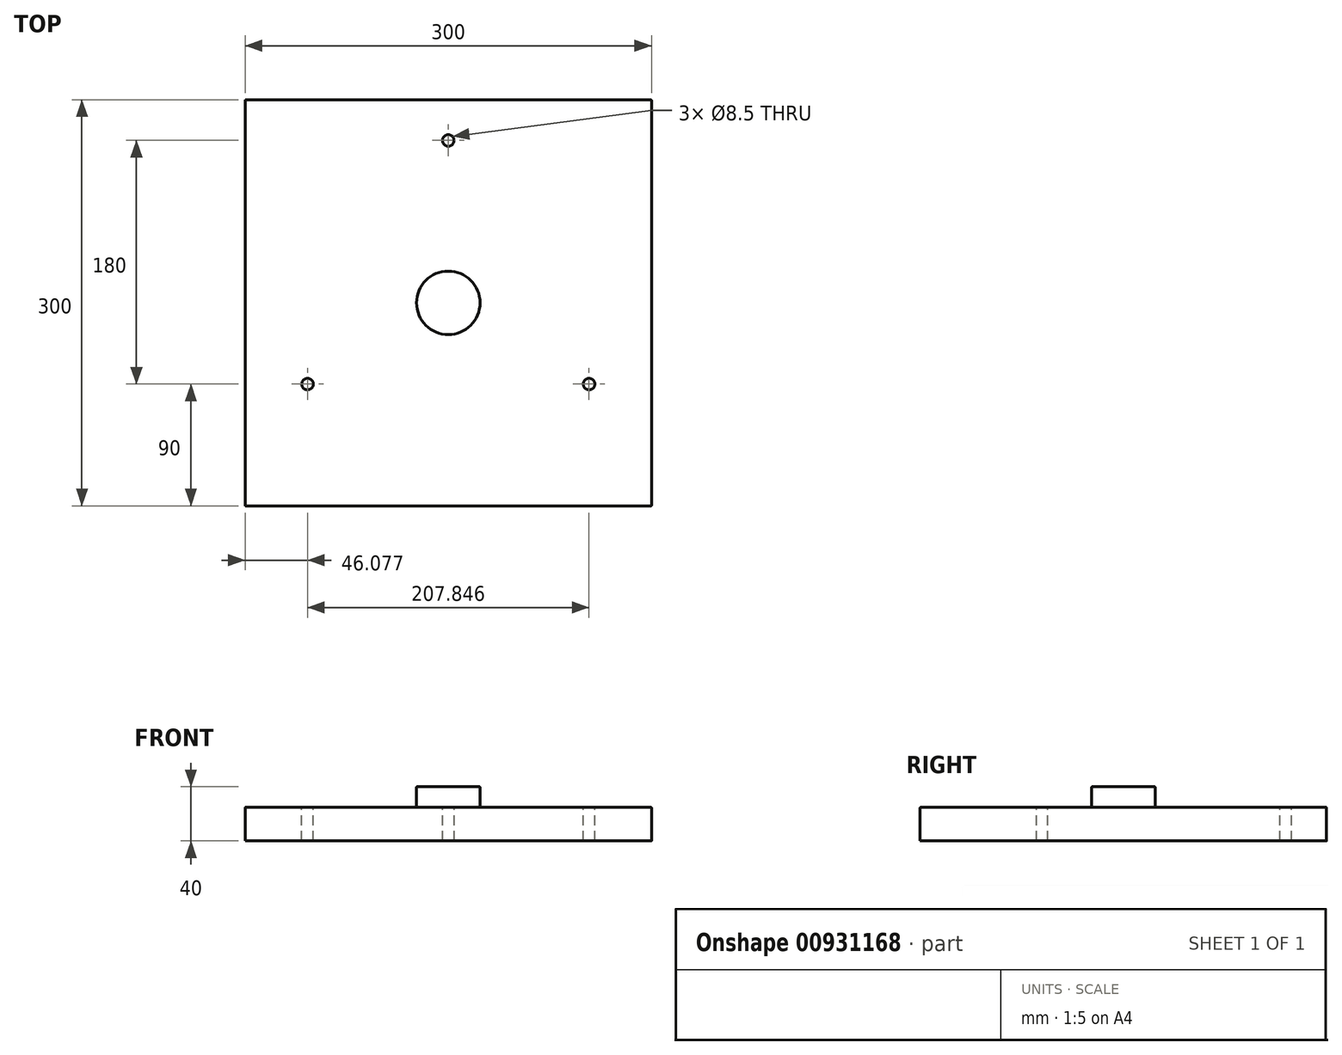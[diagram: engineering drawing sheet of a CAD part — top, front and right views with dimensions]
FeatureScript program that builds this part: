
annotation { "Feature Type Name" : "Feature", "Feature Type Description" : "" }
export const myFeature = defineFeature(function(context is Context, id is Id, definition is map)
    precondition{}
    {
        {
            var Q0;
            Q0=qCreatedBy(makeId("Top.planeOp"),FACE);
            var sketch = newSketch(context, id + "F0", { "sketchPlane" : qUnion([Q0])});
            skLineSegment(sketch, "E0.bottom", {"start": v(150, 150) * mm, "end": v(-150, 150) * mm});
            skLineSegment(sketch, "E0.top", {"start": v(150, -150) * mm, "end": v(-150, -150) * mm});
            skLineSegment(sketch, "E0.left", {"start": v(150, 150) * mm, "end": v(150, -150) * mm});
            skLineSegment(sketch, "E0.right", {"start": v(-150, 150) * mm, "end": v(-150, -150) * mm});
            skPoint(sketch, "E0.middle", {"position": v(0, 0) * mm});
            skSolve(sketch);
        }
        {
            var Q0;
            Q0=makeQuery(id+"F0.imprint","IMPRINT",FACE,{"disambiguationData":[TD([[makeQuery(id+"F0.imprint","IMPRINT",EDGE,{"derivedFrom":sQuery(id+"F0.wireOp",EDGE,"E0.bottom")}),1.0]])]});
            extrude(context, id + "F1", {"entities" : qUnion([Q0]), "depth" : 25 * mm, "offsetDistance" : 25 * mm});
        }
        {
            var Q0;
            Q0=makeQuery(id+"F1.opExtrude","CAP_FACE",FACE,{"disambiguationData":[OSD([sQuery(id+"F0.wireOp",EDGE,"E0.bottom"),sQuery(id+"F0.wireOp",EDGE,"E0.top"),sQuery(id+"F0.wireOp",EDGE,"E0.left"),sQuery(id+"F0.wireOp",EDGE,"E0.right")])],"isStart":false});
            var sketch = newSketch(context, id + "F2", { "sketchPlane" : qUnion([Q0])});
            skCircle(sketch, "E1", {"center": v(0, 0) * mm, "radius": 23.45 * mm});
            skSolve(sketch);
        }
        {
            var Q0;
            Q0=makeQuery(id+"F2.imprint","IMPRINT",FACE,{"disambiguationData":[TD([[makeQuery(id+"F2.imprint","IMPRINT",EDGE,{"derivedFrom":sQuery(id+"F2.wireOp",EDGE,"E1")}),1.0]])]});
            extrude(context, id + "F3", {"entities" : qUnion([Q0]), "operationType" : NewBodyOperationType.ADD, "depth" : 15 * mm, "offsetDistance" : 25 * mm});
        }
        {
            var Q0;
            Q0=makeQuery(id+"F1.opExtrude","CAP_FACE",FACE,{"disambiguationData":[OSD([sQuery(id+"F0.wireOp",EDGE,"E0.bottom"),sQuery(id+"F0.wireOp",EDGE,"E0.top"),sQuery(id+"F0.wireOp",EDGE,"E0.left"),sQuery(id+"F0.wireOp",EDGE,"E0.right")])],"isStart":false});
            var sketch = newSketch(context, id + "F4", { "sketchPlane" : qUnion([Q0])});
            skCircle(sketch, "E2", {"center": v(0, 0) * mm, "radius": 120 * mm, "construction": true});
            skLineSegment(sketch, "E3", {"start": v(0, 0) * mm, "end": v(0, 132.8) * mm, "construction": true});
            skLineSegment(sketch, "E4", {"start": v(0, 0) * mm, "end": v(127.4, -73.56) * mm, "construction": true});
            skLineSegment(sketch, "E5", {"start": v(0, 0) * mm, "end": v(-131.87, -76.14) * mm, "construction": true});
            skPoint(sketch, "E6", {"position": v(0, 120) * mm});
            skPoint(sketch, "E7", {"position": v(103.92, -60) * mm});
            skPoint(sketch, "E8", {"position": v(-103.92, -60) * mm});
            skSolve(sketch);
        }
        {
            var Q0;
            Q0=sQuery(id+"F4.wireOp",VERTEX,"E6");
            var Q1;
            Q1=sQuery(id+"F4.wireOp",VERTEX,"E7");
            var Q2;
            Q2=sQuery(id+"F4.wireOp",VERTEX,"E8");
            var Q3;
            Q3=makeQuery(id+"F1.opExtrude","SWEPT_BODY",BODY,{"disambiguationData":[OSD([sQuery(id+"F0.wireOp",EDGE,"E0.bottom"),sQuery(id+"F0.wireOp",EDGE,"E0.top"),sQuery(id+"F0.wireOp",EDGE,"E0.left"),sQuery(id+"F0.wireOp",EDGE,"E0.right")])]});
            hole(context, id + "F5", {"style" : HoleStyle.SIMPLE, "endStyle" : HoleEndStyle.THROUGH, "standardTappedOrClearance" : lookupTablePath({ "standard" : "ISO", "engagement" : "75%", "pitch" : "1.5 mm", "size" : "M10", "type" : "Tapped" }), "standardBlindInLast" : lookupTablePath({ "standard" : "ISO", "engagement" : "75%", "pitch" : "1.5 mm", "size" : "M10", "type" : "Tapped" }), "holeDiameter" : 8.5 * mm, "majorDiameter" : 10 * mm, "showTappedDepth" : true, "isTappedThrough" : true, "tappedDepth" : 12 * mm, "tapClearance" : 3, "locations" : qUnion([Q0, Q1, Q2]), "scope" : qUnion([Q3])});
        }
        {
            var Q0;
            Q0=makeQuery(id+"F3.opExtrude","CAP_EDGE",EDGE,{"disambiguationData":[OSD([sQuery(id+"F2.wireOp",EDGE,"E1")])],"isStart":false});
            var Q1;
            Q1=makeQuery(id+"F1.opExtrude","CAP_FACE",FACE,{"disambiguationData":[OSD([sQuery(id+"F0.wireOp",EDGE,"E0.bottom"),sQuery(id+"F0.wireOp",EDGE,"E0.top"),sQuery(id+"F0.wireOp",EDGE,"E0.left"),sQuery(id+"F0.wireOp",EDGE,"E0.right")])],"isStart":false});
            var Q2;
            Q2=makeQuery(id+"F1.opExtrude","SWEPT_EDGE",EDGE,{"disambiguationData":[OSD([sQuery(id+"F0.wireOp",EDGE,"E0.top"),sQuery(id+"F0.wireOp",EDGE,"E0.left")])]});
            var Q3;
            Q3=makeQuery(id+"F1.opExtrude","SWEPT_EDGE",EDGE,{"disambiguationData":[OSD([sQuery(id+"F0.wireOp",EDGE,"E0.bottom"),sQuery(id+"F0.wireOp",EDGE,"E0.left")])]});
            var Q4;
            Q4=makeQuery(id+"F1.opExtrude","SWEPT_EDGE",EDGE,{"disambiguationData":[OSD([sQuery(id+"F0.wireOp",EDGE,"E0.top"),sQuery(id+"F0.wireOp",EDGE,"E0.right")])]});
            var Q5;
            Q5=makeQuery(id+"F1.opExtrude","SWEPT_EDGE",EDGE,{"disambiguationData":[OSD([sQuery(id+"F0.wireOp",EDGE,"E0.bottom"),sQuery(id+"F0.wireOp",EDGE,"E0.right")])]});
            fillet(context, id + "F6", {"entities" : qUnion([Q0, Q1, Q2, Q3, Q4, Q5]), "radius" : 0.5 * mm, "tangentPropagation" : true, "allowEdgeOverflow" : false});
        }
    });
